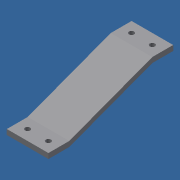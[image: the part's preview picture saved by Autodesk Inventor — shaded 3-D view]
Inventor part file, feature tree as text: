
AUTODESK INVENTOR PART (.ipt)
format: ipt  version: 2021 (Build 250183000, 183)  size: 110,080 bytes
history: native  units: mm
features: extrude x2, sketch x2
ambient origin geometry x8: Origin, YZ Plane, XZ Plane, XY Plane, X Axis, Y Axis, Z Axis, Center Point
bodies: Solid1 (feature_tree)
feature tree (4):
  extrude  "Extrusion1"  Depth=20.0mm
  extrude  "Extrusion2"  Depth=20.0mm
  sketch  "Sketch1"  dims[d0=5.0mm d1=20.0mm]
  sketch  "Sketch2"  dims[d2=5.0mm d3=20.0mm d4=35.0mm d5=120.0mm d6=40.0mm d7=0.0mm d8=5.0mm d9=5.0mm d10=5.0mm d11=5.0mm d12=10.0mm d13=10.0mm d14=10.0mm d15=10.0mm d16=10.0mm d17=10.0mm d18=10.0mm d19=10.0mm d20=90.0mm d21=0.0mm]
